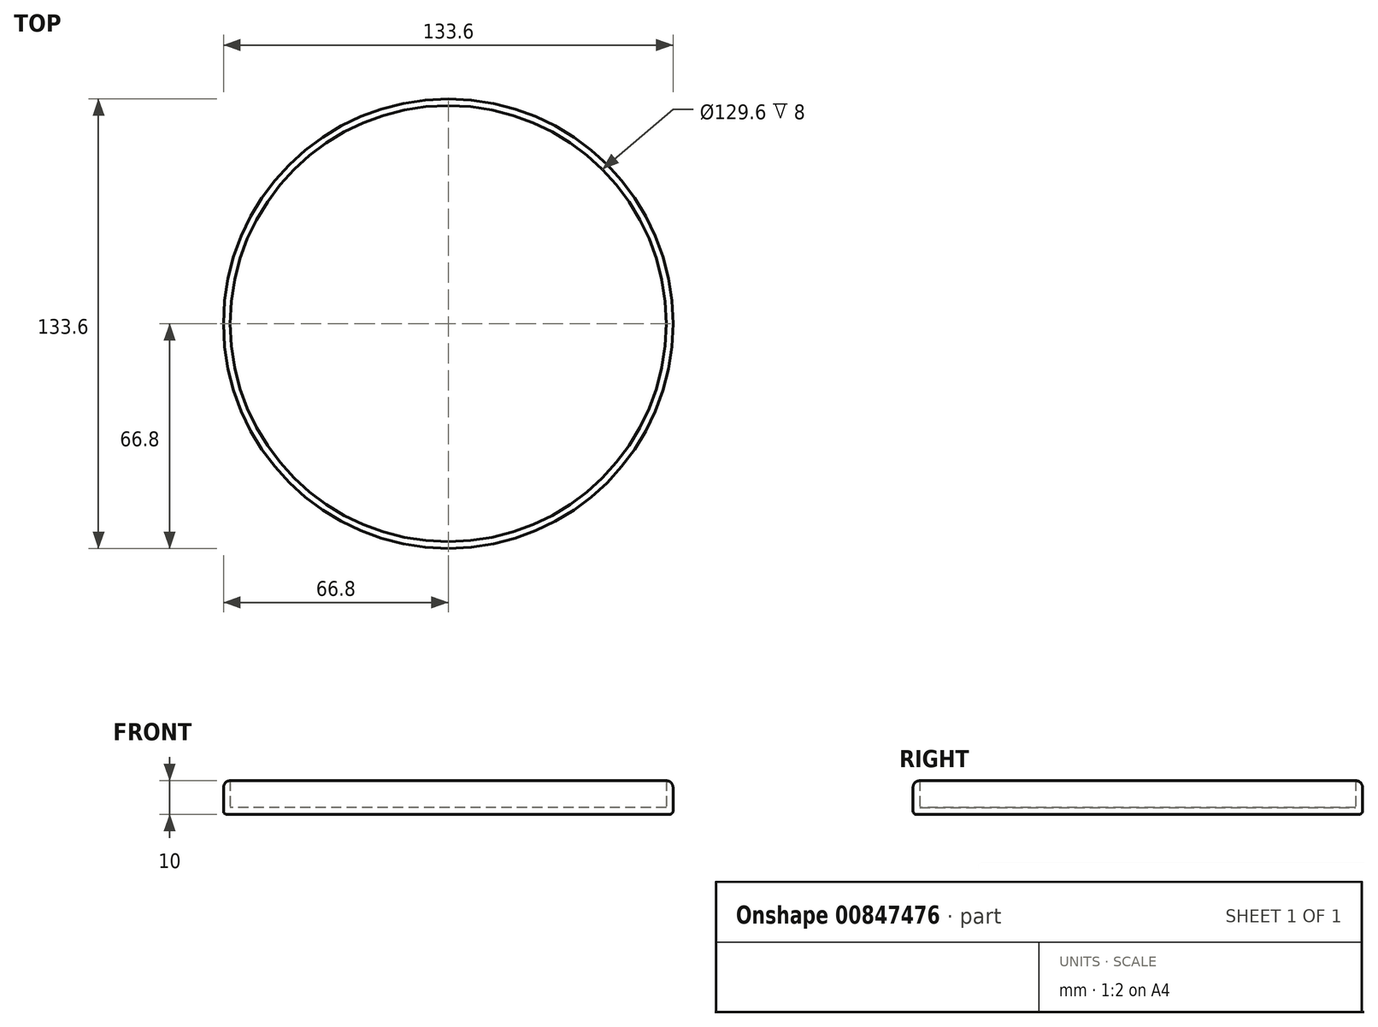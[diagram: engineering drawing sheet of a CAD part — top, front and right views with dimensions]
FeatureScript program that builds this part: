
annotation { "Feature Type Name" : "Feature", "Feature Type Description" : "" }
export const myFeature = defineFeature(function(context is Context, id is Id, definition is map)
    precondition{}
    {
        {
            var Q0;
            Q0=qCreatedBy(makeId("Top.planeOp"),FACE);
            var sketch = newSketch(context, id + "F0", { "sketchPlane" : qUnion([Q0])});
            skCircle(sketch, "E0", {"center": v(0, 0) * mm, "radius": 66.8 * mm});
            skSolve(sketch);
        }
        {
            var Q0;
            Q0 = qSketchRegion(id + "F0", true);
            extrude(context, id + "F1", {"entities" : qUnion([Q0]), "depth" : 2 * mm, "offsetDistance" : 25 * mm});
        }
        {
            var Q0;
            Q0=makeQuery(id+"F1.opExtrude","CAP_FACE",FACE,{"disambiguationData":[OSD([sQuery(id+"F0.wireOp",EDGE,"E0")])],"isStart":false});
            var sketch = newSketch(context, id + "F2", { "sketchPlane" : qUnion([Q0])});
            skCircle(sketch, "E1", {"center": v(0, 0) * mm, "radius": 66.8 * mm});
            skCircle(sketch, "E2", {"center": v(0, 0) * mm, "radius": 64.8 * mm});
            skSolve(sketch);
        }
        {
            var Q0;
            Q0 = qSketchRegion(id + "F2", true);
            extrude(context, id + "F3", {"entities" : qUnion([Q0]), "operationType" : NewBodyOperationType.ADD, "depth" : 8 * mm, "offsetDistance" : 25 * mm});
        }
        {
            var Q0;
            Q0=makeQuery(id+"F1.opExtrude","CAP_EDGE",EDGE,{"disambiguationData":[OSD([sQuery(id+"F0.wireOp",EDGE,"E0")])],"isStart":true});
            var Q1;
            Q1=makeQuery(id+"F3.opExtrude","CAP_EDGE",EDGE,{"disambiguationData":[OSD([sQuery(id+"F2.wireOp",EDGE,"E2")])],"isStart":true});
            fillet(context, id + "F4", {"entities" : qUnion([Q0, Q1]), "radius" : 1 * mm, "tangentPropagation" : true, "allowEdgeOverflow" : false});
        }
        {
            var Q0;
            Q0=makeQuery(id+"F3.opExtrude","CAP_EDGE",EDGE,{"disambiguationData":[OSD([sQuery(id+"F2.wireOp",EDGE,"E1")])],"isStart":false});
            fillet(context, id + "F5", {"entities" : qUnion([Q0]), "radius" : 2 * mm, "tangentPropagation" : true, "allowEdgeOverflow" : false});
        }
    });
